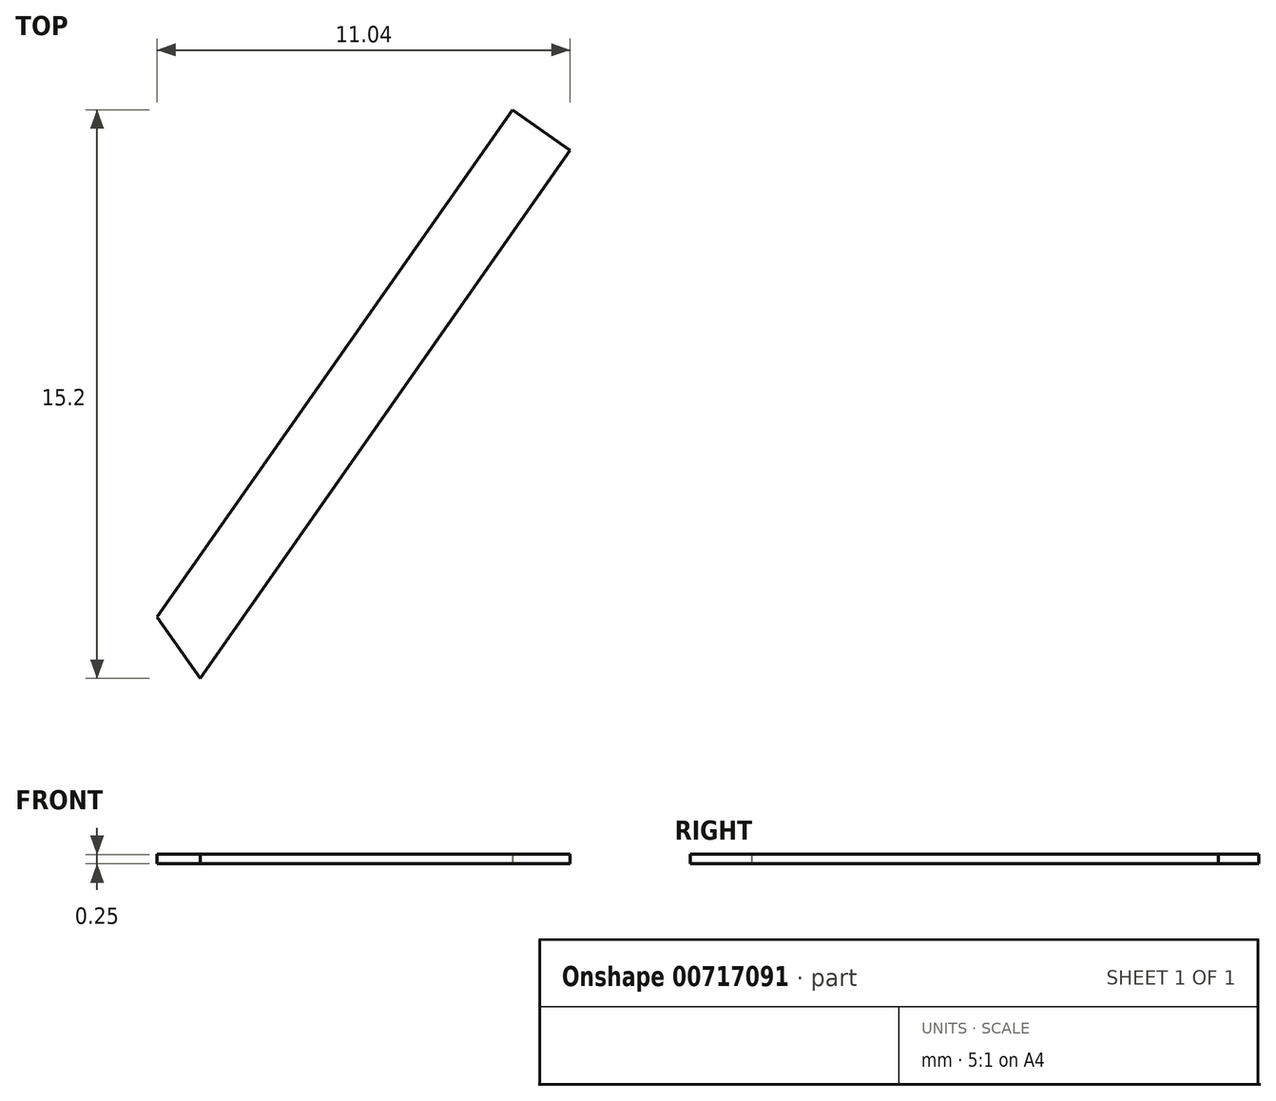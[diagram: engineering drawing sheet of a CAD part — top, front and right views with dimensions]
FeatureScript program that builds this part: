
annotation { "Feature Type Name" : "Feature", "Feature Type Description" : "" }
export const myFeature = defineFeature(function(context is Context, id is Id, definition is map)
    precondition{}
    {
        {
            var Q0;
            Q0=qCreatedBy(makeId("Top.planeOp"),FACE);
            var sketch = newSketch(context, id + "F0", { "sketchPlane" : qUnion([Q0])});
            skLineSegment(sketch, "E0", {"start": v(0, 0) * mm, "end": v(9.5, 13.55) * mm});
            skLineSegment(sketch, "E1", {"start": v(9.5, 13.55) * mm, "end": v(11.04, 12.47) * mm});
            skLineSegment(sketch, "E2", {"start": v(11.04, 12.47) * mm, "end": v(1.15, -1.65) * mm});
            skLineSegment(sketch, "E3", {"start": v(1.15, -1.65) * mm, "end": v(0, 0) * mm});
            skSolve(sketch);
        }
        {
            var Q0;
            Q0=makeQuery(id+"F0.imprint","IMPRINT",FACE,{"disambiguationData":[TD([[makeQuery(id+"F0.imprint","IMPRINT",EDGE,{"derivedFrom":sQuery(id+"F0.wireOp",EDGE,"E0")}),-1.0]])]});
            extrude(context, id + "F1", {"entities" : qUnion([Q0]), "depth" : 0.25 * mm, "offsetDistance" : 25.4 * mm});
        }
    });
